# Revit family: Drain-Grates_MultiDrain_AlfaChannel-CatchBasin
name_source: partatom
category: Site
units: mm (PartAtom-declared; Revit-internal decimal feet)

## family parameters
Classification Number = 23.10.10.12
Cut with Voids When Loaded = No
Host = Face
Part Type = Normal
Round Connector Dimension = Use Diameter
Shared = Yes

## types (2) — shared parameters
ADA Compliant = No
Assembly Code = A1030600
Capacity = Load Rating as Specified
Construction Details = http://www.arcat.com
Default Elevation = 0' - 0"
Description = MultiDrain Product as Specified
Frame Finish = Metal - MultiDrain - Black Paint Grating
Keynote = 02600
Manufacturer = MultiDrain Systems
Manufacturer Fax = 704-508-1011
Manufacturer Website = http://www.multidrainsystems.com
Model = As Specified
Product Data = http://www.arcat.com
Revision = R1_12_2013
Sales Information = http://www.multidrainsystems.com
Send Message = http://www.arcat.com
Specification = http://www.arcat.com
URL = http://www.multidrainsystems.com
zero-valued in all types: Expected Lifespan (Years), Maintenance Schedule (Months), Open Area, Warranty Duration (Years)

## per-type parameters (varying)
| type | FramedGrate | Grate Width |
| Default AlfaChannelCatchBasin InlayGrate | No | 1' - 0 3/16" |
| Default AlfaChannelCatchBasin FramedGrate | Yes | 0' - 4 15/16" |

## geometry (parser evidence)
native form markers: Sweep x2
no freeform markers — native parametric forms only
